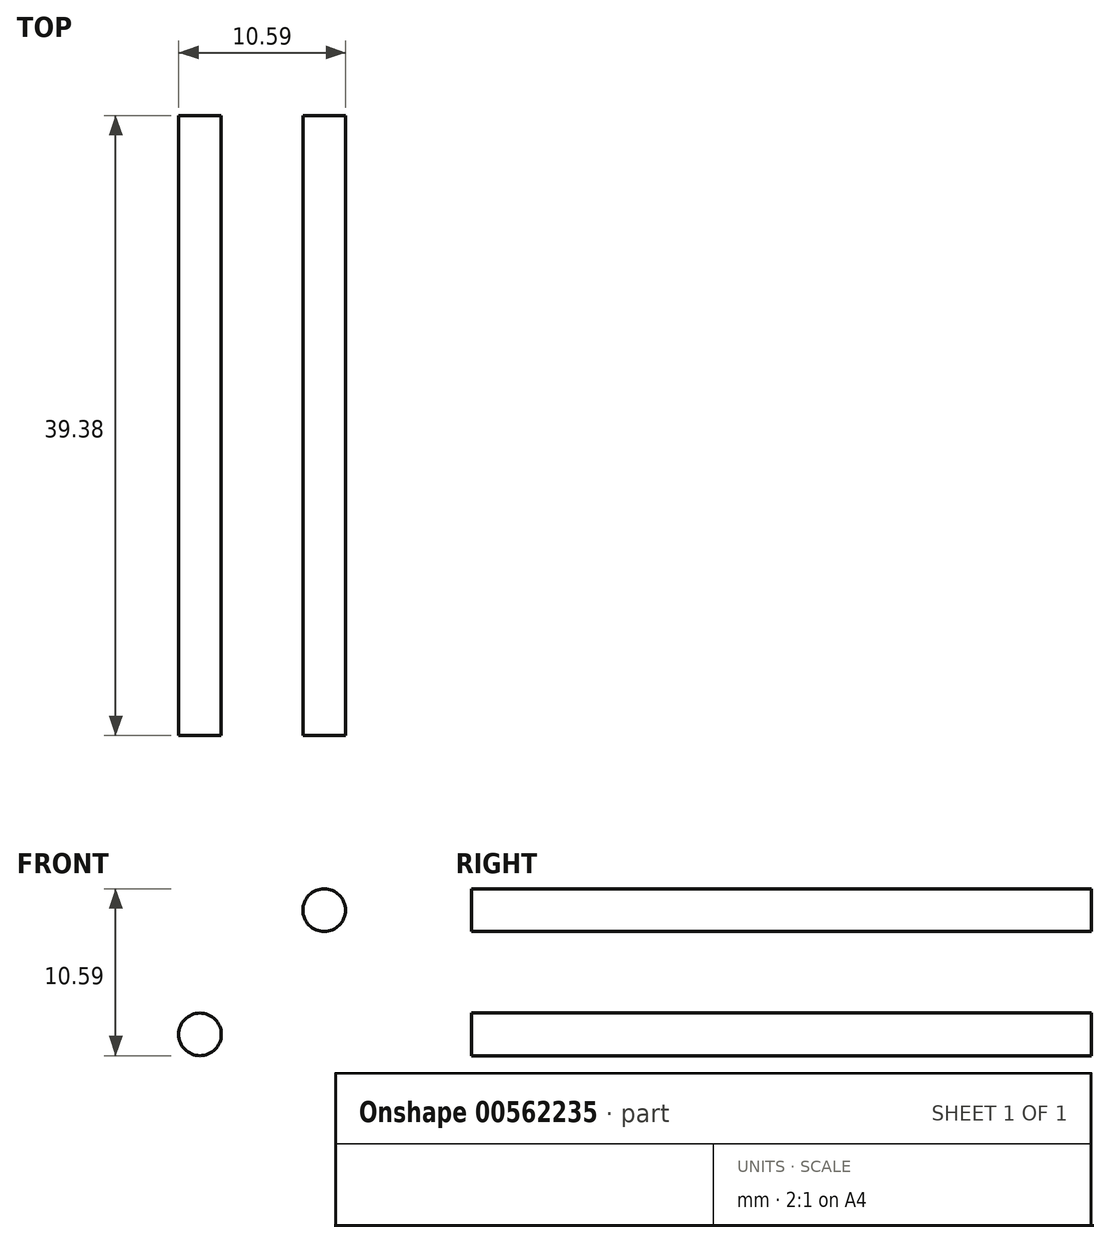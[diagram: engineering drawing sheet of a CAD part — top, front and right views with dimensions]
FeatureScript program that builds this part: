
annotation { "Feature Type Name" : "Feature", "Feature Type Description" : "" }
export const myFeature = defineFeature(function(context is Context, id is Id, definition is map)
    precondition{}
    {
        {
            var Q0;
            Q0=qCreatedBy(makeId("Front.planeOp"),FACE);
            var sketch = newSketch(context, id + "F0", { "sketchPlane" : qUnion([Q0])});
            skCircle(sketch, "E0", {"center": v(0, 0) * mm, "radius": 19.05 * mm});
            skCircle(sketch, "E1", {"center": v(0, 0) * mm, "radius": 22.23 * mm});
            skSolve(sketch);
        }
        {
            var Q0;
            Q0=makeQuery(id+"F0.imprint","IMPRINT",FACE,{"disambiguationData":[TD([[makeQuery(id+"F0.imprint","IMPRINT",EDGE,{"derivedFrom":sQuery(id+"F0.wireOp",EDGE,"E0")}),1.0]])]});
            extrude(context, id + "F1", {"entities" : qUnion([Q0]), "depth" : 13.33 * mm, "offsetDistance" : 25.4 * mm, "hasSecondDirection" : true, "secondDirectionOppositeDirection" : true, "secondDirectionDepth" : 13.33 * mm});
        }
        {
            var Q0;
            Q0=makeQuery(id+"F1.opExtrude","CAP_FACE",FACE,{"disambiguationData":[OSD([sQuery(id+"F0.wireOp",EDGE,"E0")])],"isStart":false});
            var sketch = newSketch(context, id + "F2", { "sketchPlane" : qUnion([Q0])});
            skCircle(sketch, "E2", {"center": v(0, 0) * mm, "radius": 22.23 * mm});
            skSolve(sketch);
        }
        {
            var Q0;
            Q0 = qSketchRegion(id + "F2", true);
            extrude(context, id + "F3", {"entities" : qUnion([Q0]), "operationType" : NewBodyOperationType.ADD, "depth" : 6.35 * mm, "offsetDistance" : 25.4 * mm});
        }
        {
            var Q0;
            Q0=makeQuery(id+"F1.opExtrude","CAP_FACE",FACE,{"disambiguationData":[OSD([sQuery(id+"F0.wireOp",EDGE,"E0")])],"isStart":true});
            var sketch = newSketch(context, id + "F4", { "sketchPlane" : qUnion([Q0])});
            skCircle(sketch, "E3", {"center": v(0, 0) * mm, "radius": 22.23 * mm});
            skSolve(sketch);
        }
        {
            var Q0;
            Q0 = qSketchRegion(id + "F4", true);
            extrude(context, id + "F5", {"entities" : qUnion([Q0]), "operationType" : NewBodyOperationType.ADD, "depth" : 6.35 * mm, "offsetDistance" : 25.4 * mm});
        }
        {
            var Q0;
            Q0=makeQuery(id+"F3.opExtrude","CAP_FACE",FACE,{"disambiguationData":[OSD([sQuery(id+"F2.wireOp",EDGE,"E2")])],"isStart":false});
            var sketch = newSketch(context, id + "F6", { "sketchPlane" : qUnion([Q0])});
            skCircle(sketch, "E4", {"center": v(0, 0) * mm, "radius": 7.89 * mm});
            skCircle(sketch, "E5", {"center": v(-7.89, 0) * mm, "radius": 1.35 * mm});
            skCircle(sketch, "E6", {"center": v(0, 0) * mm, "radius": 2.35 * mm});
            skCircle(sketch, "E7", {"center": v(0, 7.89) * mm, "radius": 1.35 * mm});
            skCircle(sketch, "E8", {"center": v(7.89, 0) * mm, "radius": 1.35 * mm});
            skCircle(sketch, "E9", {"center": v(0, -7.89) * mm, "radius": 1.35 * mm});
            skSolve(sketch);
        }
        {
            var Q0;
            {var subQ0=sQuery(id+"F6.wireOp",EDGE,"E5");var subQ1=sQuery(id+"F6.wireOp",EDGE,"E4");var subQ2=makeQuery(id+"F6.imprint","INTERSECT",VERTEX,{"disambiguationData":[OD(0.0)],"derivedFrom":[subQ1,subQ0]});Q0=makeQuery(id+"F6.imprint","IMPRINT",FACE,{"disambiguationData":[TD([[makeQuery(id+"F6.imprint","IMPRINT",EDGE,{"disambiguationData":[TD([[subQ2,-1.0]])],"derivedFrom":subQ1}),1.0]])]});}
            var Q1;
            {var subQ0=sQuery(id+"F6.wireOp",EDGE,"E5");var subQ1=sQuery(id+"F6.wireOp",EDGE,"E4");var subQ2=makeQuery(id+"F6.imprint","INTERSECT",VERTEX,{"disambiguationData":[OD(0.0)],"derivedFrom":[subQ1,subQ0]});Q1=makeQuery(id+"F6.imprint","IMPRINT",FACE,{"disambiguationData":[TD([[makeQuery(id+"F6.imprint","IMPRINT",EDGE,{"disambiguationData":[TD([[subQ2,-1.0]])],"derivedFrom":subQ1}),-1.0]])]});}
            var Q2;
            {var subQ0=sQuery(id+"F6.wireOp",EDGE,"E8");var subQ1=sQuery(id+"F6.wireOp",EDGE,"E4");var subQ2=makeQuery(id+"F6.imprint","INTERSECT",VERTEX,{"disambiguationData":[OD(0.0)],"derivedFrom":[subQ1,subQ0]});Q2=makeQuery(id+"F6.imprint","IMPRINT",FACE,{"disambiguationData":[TD([[makeQuery(id+"F6.imprint","IMPRINT",EDGE,{"disambiguationData":[TD([[subQ2,1.0]])],"derivedFrom":subQ1}),1.0]])]});}
            var Q3;
            {var subQ0=sQuery(id+"F6.wireOp",EDGE,"E8");var subQ1=sQuery(id+"F6.wireOp",EDGE,"E4");var subQ2=makeQuery(id+"F6.imprint","INTERSECT",VERTEX,{"disambiguationData":[OD(0.0)],"derivedFrom":[subQ1,subQ0]});Q3=makeQuery(id+"F6.imprint","IMPRINT",FACE,{"disambiguationData":[TD([[makeQuery(id+"F6.imprint","IMPRINT",EDGE,{"disambiguationData":[TD([[subQ2,1.0]])],"derivedFrom":subQ1}),-1.0]])]});}
            var Q4;
            Q4=makeQuery(id+"F6.imprint","IMPRINT",FACE,{"disambiguationData":[TD([[makeQuery(id+"F6.imprint","IMPRINT",EDGE,{"derivedFrom":sQuery(id+"F6.wireOp",EDGE,"E6")}),1.0]])]});
            var Q5;
            {var subQ0=sQuery(id+"F6.wireOp",EDGE,"E9");var subQ1=sQuery(id+"F6.wireOp",EDGE,"E4");var subQ2=makeQuery(id+"F6.imprint","INTERSECT",VERTEX,{"disambiguationData":[OD(0.0)],"derivedFrom":[subQ1,subQ0]});Q5=makeQuery(id+"F6.imprint","IMPRINT",FACE,{"disambiguationData":[TD([[makeQuery(id+"F6.imprint","IMPRINT",EDGE,{"disambiguationData":[TD([[subQ2,-1.0]])],"derivedFrom":subQ1}),1.0]])]});}
            var Q6;
            {var subQ0=sQuery(id+"F6.wireOp",EDGE,"E9");var subQ1=sQuery(id+"F6.wireOp",EDGE,"E4");var subQ2=makeQuery(id+"F6.imprint","INTERSECT",VERTEX,{"disambiguationData":[OD(0.0)],"derivedFrom":[subQ1,subQ0]});Q6=makeQuery(id+"F6.imprint","IMPRINT",FACE,{"disambiguationData":[TD([[makeQuery(id+"F6.imprint","IMPRINT",EDGE,{"disambiguationData":[TD([[subQ2,-1.0]])],"derivedFrom":subQ1}),-1.0]])]});}
            var Q7;
            {var subQ0=sQuery(id+"F6.wireOp",EDGE,"E7");var subQ1=sQuery(id+"F6.wireOp",EDGE,"E4");var subQ2=makeQuery(id+"F6.imprint","INTERSECT",VERTEX,{"disambiguationData":[OD(0.0)],"derivedFrom":[subQ1,subQ0]});Q7=makeQuery(id+"F6.imprint","IMPRINT",FACE,{"disambiguationData":[TD([[makeQuery(id+"F6.imprint","IMPRINT",EDGE,{"disambiguationData":[TD([[subQ2,-1.0]])],"derivedFrom":subQ1}),1.0]])]});}
            var Q8;
            {var subQ0=sQuery(id+"F6.wireOp",EDGE,"E7");var subQ1=sQuery(id+"F6.wireOp",EDGE,"E4");var subQ2=makeQuery(id+"F6.imprint","INTERSECT",VERTEX,{"disambiguationData":[OD(0.0)],"derivedFrom":[subQ1,subQ0]});Q8=makeQuery(id+"F6.imprint","IMPRINT",FACE,{"disambiguationData":[TD([[makeQuery(id+"F6.imprint","IMPRINT",EDGE,{"disambiguationData":[TD([[subQ2,-1.0]])],"derivedFrom":subQ1}),-1.0]])]});}
            extrude(context, id + "F7", {"entities" : qUnion([Q0, Q1, Q2, Q3, Q4, Q5, Q6, Q7, Q8]), "operationType" : NewBodyOperationType.REMOVE, "oppositeDirection" : true, "depth" : 39.37 * mm, "offsetDistance" : 25.4 * mm});
        }
    });
